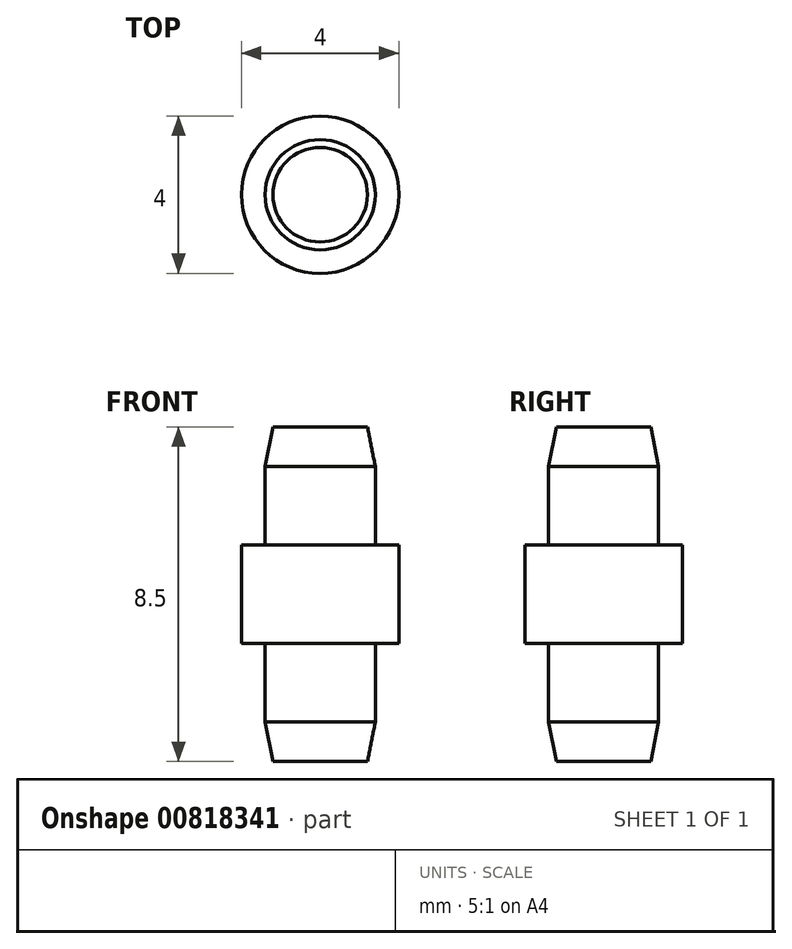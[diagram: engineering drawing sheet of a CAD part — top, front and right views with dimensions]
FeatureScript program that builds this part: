
annotation { "Feature Type Name" : "Feature", "Feature Type Description" : "" }
export const myFeature = defineFeature(function(context is Context, id is Id, definition is map)
    precondition{}
    {
        {
            var Q0;
            Q0=qCreatedBy(makeId("Top.planeOp"),FACE);
            var sketch = newSketch(context, id + "F0", { "sketchPlane" : qUnion([Q0])});
            skCircle(sketch, "E0", {"center": v(0, 0) * mm, "radius": 1.4 * mm});
            skSolve(sketch);
        }
        {
            var Q0;
            Q0=makeQuery(id+"F0.imprint","IMPRINT",FACE,{"disambiguationData":[TD([[makeQuery(id+"F0.imprint","IMPRINT",EDGE,{"derivedFrom":sQuery(id+"F0.wireOp",EDGE,"E0")}),1.0]])]});
            extrude(context, id + "F1", {"entities" : qUnion([Q0]), "depth" : 3 * mm, "offsetDistance" : 25 * mm});
        }
        {
            var Q0;
            Q0=makeQuery(id+"F1.opExtrude","CAP_FACE",FACE,{"disambiguationData":[OSD([sQuery(id+"F0.wireOp",EDGE,"E0")])],"isStart":false});
            var sketch = newSketch(context, id + "F2", { "sketchPlane" : qUnion([Q0])});
            skCircle(sketch, "E1", {"center": v(0, 0) * mm, "radius": 2 * mm});
            skSolve(sketch);
        }
        {
            var Q0;
            Q0=makeQuery(id+"F2.imprint","IMPRINT",FACE,{"disambiguationData":[TD([[makeQuery(id+"F2.imprint","IMPRINT",EDGE,{"derivedFrom":sQuery(id+"F2.wireOp",EDGE,"E1")}),1.0]])]});
            var Q1;
            Q1=makeQuery(id+"F2.imprint","IMPRINT",FACE,{"disambiguationData":[TD([[makeQuery(id+"F2.imprint","IMPRINT",EDGE,{"derivedFrom":makeQuery(id+"F1.opExtrude","CAP_EDGE",EDGE,{"disambiguationData":[OSD([sQuery(id+"F0.wireOp",EDGE,"E0")])],"isStart":false})}),1.0]])]});
            extrude(context, id + "F3", {"entities" : qUnion([Q0, Q1]), "depth" : 2.5 * mm, "offsetDistance" : 25 * mm});
        }
        {
            var Q0;
            Q0=makeQuery(id+"F3.opExtrude","CAP_FACE",FACE,{"disambiguationData":[OSD([sQuery(id+"F2.wireOp",EDGE,"E1")])],"isStart":false});
            var sketch = newSketch(context, id + "F4", { "sketchPlane" : qUnion([Q0])});
            skCircle(sketch, "E2", {"center": v(0, 0) * mm, "radius": 1.4 * mm});
            skSolve(sketch);
        }
        {
            var Q0;
            Q0=makeQuery(id+"F4.imprint","IMPRINT",FACE,{"disambiguationData":[TD([[makeQuery(id+"F4.imprint","IMPRINT",EDGE,{"derivedFrom":sQuery(id+"F4.wireOp",EDGE,"E2")}),1.0]])]});
            extrude(context, id + "F5", {"entities" : qUnion([Q0]), "operationType" : NewBodyOperationType.ADD, "depth" : 3 * mm, "offsetDistance" : 25 * mm});
        }
        {
            var Q0;
            Q0=makeQuery(id+"F5.opExtrude","CAP_EDGE",EDGE,{"disambiguationData":[OSD([sQuery(id+"F4.wireOp",EDGE,"E2")])],"isStart":false});
            chamfer(context, id + "F6", {"entities" : qUnion([Q0]), "chamferType" : ChamferType.TWO_OFFSETS, "width1" : .2 * mm, "oppositeDirection" : false, "width2" : 1 * mm, "tangentPropagation" : true});
        }
        {
            var Q0;
            Q0=makeQuery(id+"F1.opExtrude","CAP_EDGE",EDGE,{"disambiguationData":[OSD([sQuery(id+"F0.wireOp",EDGE,"E0")])],"isStart":true});
            chamfer(context, id + "F7", {"entities" : qUnion([Q0]), "chamferType" : ChamferType.TWO_OFFSETS, "width1" : 1 * mm, "oppositeDirection" : false, "width2" : .2 * mm, "tangentPropagation" : true});
        }
    });
